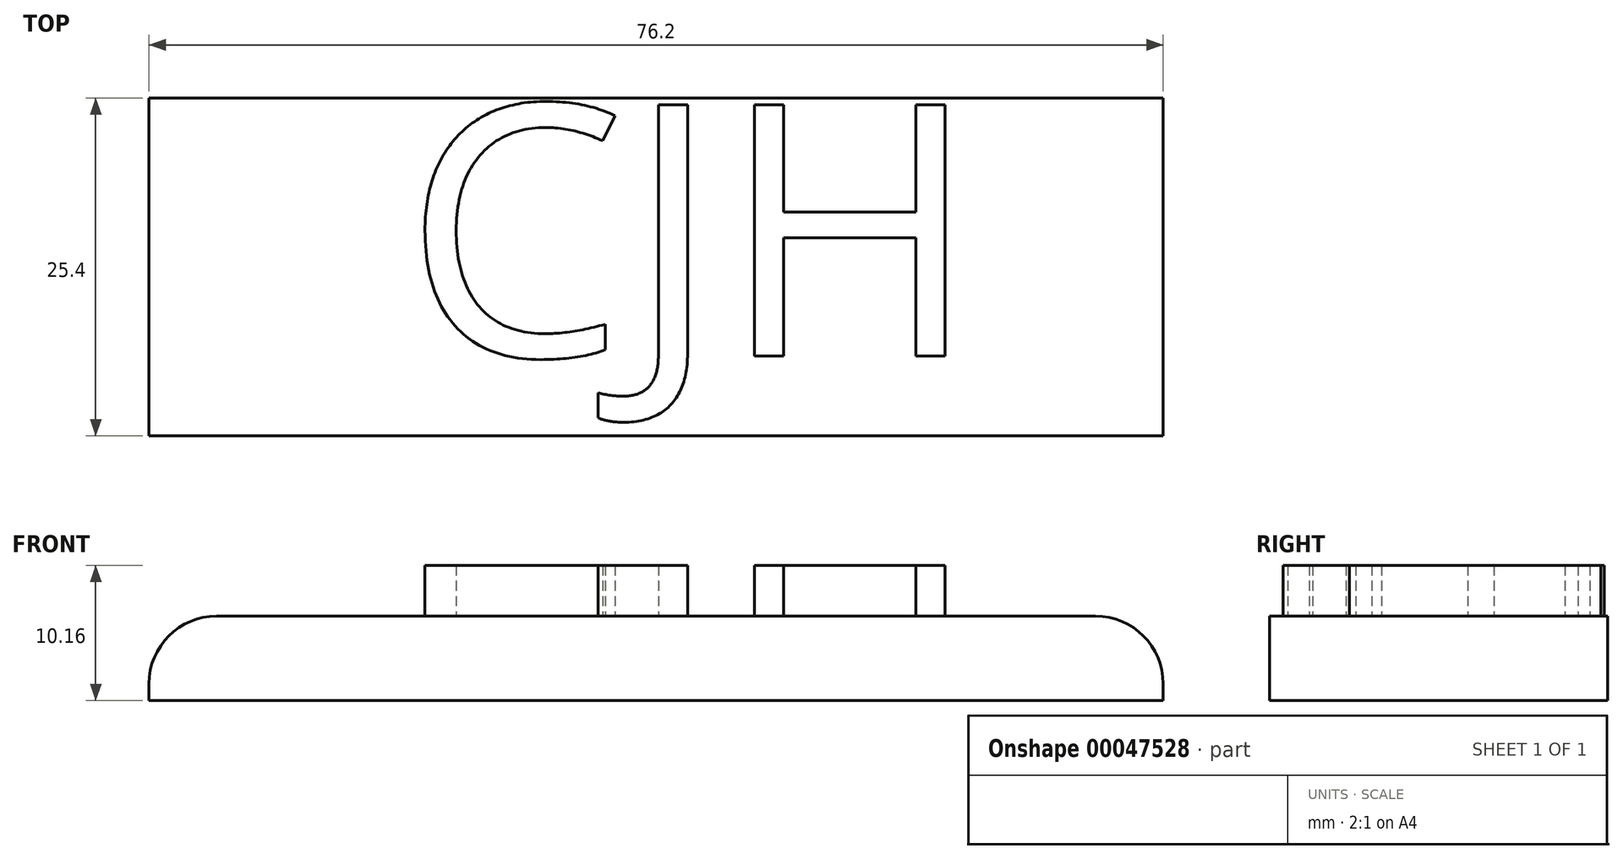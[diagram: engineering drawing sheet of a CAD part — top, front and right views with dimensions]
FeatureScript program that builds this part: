
annotation { "Feature Type Name" : "Feature", "Feature Type Description" : "" }
export const myFeature = defineFeature(function(context is Context, id is Id, definition is map)
    precondition{}
    {
        {
            var Q0;
            Q0=qCreatedBy(makeId("Top.planeOp"),FACE);
            var sketch = newSketch(context, id + "F0", { "sketchPlane" : qUnion([Q0])});
            skLineSegment(sketch, "E0.rect.bottom", {"start": v(-38.1, 12.7) * mm, "end": v(38.1, 12.7) * mm});
            skLineSegment(sketch, "E0.rect.top", {"start": v(-38.1, -12.7) * mm, "end": v(38.1, -12.7) * mm});
            skLineSegment(sketch, "E0.rect.left", {"start": v(-38.1, 12.7) * mm, "end": v(-38.1, -12.7) * mm});
            skLineSegment(sketch, "E0.rect.right", {"start": v(38.1, 12.7) * mm, "end": v(38.1, -12.7) * mm});
            skPoint(sketch, "E0.rect.middle", {"position": v(0, 0) * mm});
            skSolve(sketch);
        }
        {
            var Q0;
            Q0=makeQuery(id+"F0.imprint","IMPRINT",FACE,{"disambiguationData":[TD([[makeQuery(id+"F0.imprint","IMPRINT",EDGE,{"derivedFrom":sQuery(id+"F0.wireOp",EDGE,"E0.rect.bottom")}),-1.0]])]});
            extrude(context, id + "F1", {"entities" : qUnion([Q0]), "depth" : 6.35 * mm});
        }
        {
            var Q0;
            Q0=qCreatedBy(makeId("Top.planeOp"),FACE);
            var sketch = newSketch(context, id + "F2", { "sketchPlane" : qUnion([Q0])});
            skText(sketch, "E1", { "text": "CJH", "fontName": "OpenSans-Regular.ttf"});
            const initialGuessF2  = {"E1": [-0.01898, -0.00671, 1, 0, 0.01905]};
            skSetInitialGuess(sketch, initialGuessF2);
            skSolve(sketch);
        }
        {
            var Q0;
            Q0 = qSketchRegion(id + "F2", true);
            extrude(context, id + "F3", {"entities" : qUnion([Q0]), "operationType" : NewBodyOperationType.ADD, "depth" : 10.16 * mm});
        }
        {
            var Q0;
            Q0=makeQuery(id+"F1.opExtrude","CAP_EDGE",EDGE,{"disambiguationData":[OSD([sQuery(id+"F0.wireOp",EDGE,"E0.rect.left")])],"isStart":false});
            var Q1;
            Q1=makeQuery(id+"F1.opExtrude","CAP_EDGE",EDGE,{"disambiguationData":[OSD([sQuery(id+"F0.wireOp",EDGE,"E0.rect.right")])],"isStart":false});
            fillet(context, id + "F4", {"entities" : qUnion([Q0, Q1]), "radius" : 5.08 * mm, "tangentPropagation" : true, "allowEdgeOverflow" : false});
        }
    });
